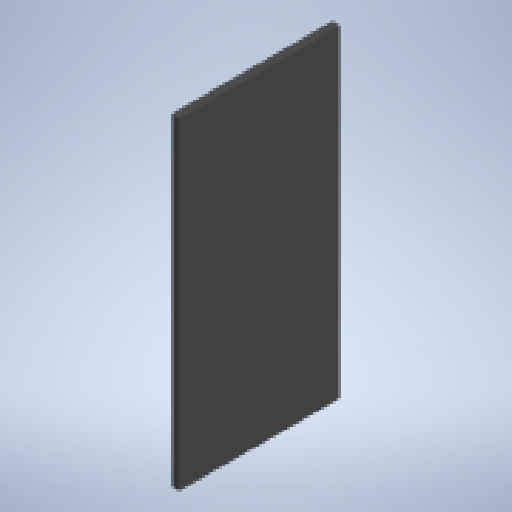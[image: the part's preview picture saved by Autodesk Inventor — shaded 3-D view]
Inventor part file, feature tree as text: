
AUTODESK INVENTOR PART (.ipt)
format: ipt  version: 2025 (Build 290162010, 162A)  size: 123,904 bytes
history: native  units: mm
features: extrude x1, sketch x1
ambient origin geometry x8: Origin, YZ Plane, XZ Plane, XY Plane, X Axis, Y Axis, Z Axis, Center Point
bodies: Volumenkörper1 (feature_tree)
feature tree (2):
  extrude  "Extrusion1"  Depth=40.0mm
  sketch  "Skizze1"  dims[d0=20.0mm d1=40.0mm d2=1.0mm d3=0.0mm]
